FCSTD DOCUMENT  (FreeCAD 0.20R29177 (Git))
Label: Top Controls
License: All rights reserved
LicenseURL: http://en.wikipedia.org/wiki/All_rights_reserved
objects: App::Link×5, App::DocumentObjectGroup×3, PartDesign::CoordinateSystem×1, App::FeaturePython×1, App::Part×1
note: 1 computed .brp shape members not serialized (recipe doc carries the construction recipe); baked Part::Feature solids carry a one-line shape summary decoded from their .brp
EXTERNAL_REF file=Top Plate.FCStd obj=LCS_Origin
EXTERNAL_REF file=Top Plate.FCStd obj=Body
EXTERNAL_REF file=Potentiometers.FCStd obj=LCS_Origin
EXTERNAL_REF file=Top Plate.FCStd obj=LCS_Potentiometers
EXTERNAL_REF file=Potentiometers.FCStd obj=Assembly
EXTERNAL_REF file=Silder.FCStd obj=LCS_Origin
EXTERNAL_REF file=Top Plate.FCStd obj=LCS_Slider
EXTERNAL_REF file=Silder.FCStd obj=Model
EXTERNAL_REF file=LCD-1.28inch.FCStd obj=LCS_Origin
EXTERNAL_REF file=Top Plate.FCStd obj=LCS_LCD
EXTERNAL_REF file=LCD-1.28inch.FCStd obj=Model
EXTERNAL_REF file=Dsub.FCStd obj=LCS_TOP
EXTERNAL_REF file=Top Plate.FCStd obj=LCS_Dsub
EXTERNAL_REF file=Dsub.FCStd obj=Body

FEATURE [App::DocumentObjectGroup] Parts
FEATURE [PartDesign::CoordinateSystem] LCS_Origin
  AttacherType = Attacher::AttachEngine3D
  MapMode = 2
  Support = -> [X_Axis]
FEATURE [App::DocumentObjectGroup] Constraints
FEATURE [App::FeaturePython] Variables  # WARN: FeaturePython — macro-defined, semantics opaque (R4)
  Type = App::PropertyContainer
FEATURE [App::DocumentObjectGroup] Configurations
FEATURE [App::Link] Top_Plate  label="Top Plate"
  AttachedBy = #LCS_Origin
  AttachedTo = Parent Assembly#LCS_Origin
  LinkedObject = -> <external Top Plate.FCStd>#Body
  SolverId = Asm4EE
  expr: Placement = LCS_Origin.Placement * AttachmentOffset * Top_Plate#LCS_Origin.Placement ^ -1
FEATURE [App::Link] Potentiometers
  AttachedBy = #LCS_Origin
  AttachedTo = Top_Plate#LCS_Potentiometers
  AttachmentOffset = pos=(0,0,0) rot=(0,0,1;1.5708rad)
  LinkPlacement = pos=(30.5,29,2) rot=(0,-1,0;3.14159rad)
  LinkedObject = -> <external Potentiometers.FCStd>#Assembly
  Placement = pos=(30.5,29,2) rot=(0,-1,0;3.14159rad)
  SolverId = Asm4EE
  expr: Placement = Top_Plate.Placement * Top_Plate#LCS_Potentiometers.Placement * AttachmentOffset * Potentiometers#LCS_Origin.Placement ^ -1
FEATURE [App::Link] Silder  label="Slider"
  AttachedBy = #LCS_Origin
  AttachedTo = Top_Plate#LCS_Slider
  AttachmentOffset = pos=(0,0,0) rot=(0,1,0;3.14159rad)
  LinkPlacement = pos=(-30.5,0,2) rot=(0,1,0;3.14159rad)
  LinkedObject = -> <external Silder.FCStd>#Model
  Placement = pos=(-30.5,0,2) rot=(0,1,0;3.14159rad)
  SolverId = Asm4EE
  expr: Placement = Top_Plate.Placement * Top_Plate#LCS_Slider.Placement * AttachmentOffset * Silder#LCS_Origin.Placement ^ -1
FEATURE [App::Link] LCD
  AttachedBy = #LCS_Origin
  AttachedTo = Top_Plate#LCS_LCD
  AttachmentOffset = pos=(0,0,0) rot=(-1,0,0;3.14159rad)
  LinkPlacement = pos=(-61.75,-15.25,2) rot=(-1,0,0;3.14159rad)
  LinkedObject = -> <external LCD-1.28inch.FCStd>#Model
  Placement = pos=(-61.75,-15.25,2) rot=(-1,0,0;3.14159rad)
  SolverId = Asm4EE
  expr: Placement = Top_Plate.Placement * Top_Plate#LCS_LCD.Placement * AttachmentOffset * LCD_1_28inch#LCS_Origin.Placement ^ -1
FEATURE [App::Link] Dsub
  AttachedBy = #LCS_TOP
  AttachedTo = Top_Plate#LCS_Dsub
  AttachmentOffset = pos=(0,0,0) rot=(0,0,1;1.5708rad)
  LinkPlacement = pos=(32.5,-21,0) rot=(0,0,1;3.14159rad)
  LinkedObject = -> <external Dsub.FCStd>#Body
  Placement = pos=(32.5,-21,0) rot=(0,0,1;3.14159rad)
  SolverId = Asm4EE
  expr: Placement = Top_Plate.Placement * Top_Plate#LCS_Dsub.Placement * AttachmentOffset * Dsub#LCS_TOP.Placement ^ -1
FEATURE [App::Part] Model
  AssemblyType = Part::Link
  Group = -> [LCS_Origin,Constraints,Variables,Configurations,Top_Plate,Potentiometers,Silder,LCD,Dsub]
  Origin = -> Origin
  Type = Assembly

RESOLVED EXTERNAL PARTS (link-assembly join: the EXTERNAL_REF files above that resolve inside this repo's crawl, each included once):
---- part Dsub.FCStd = doc fcstd_46d8f76f5e4a ----
FCSTD DOCUMENT  (FreeCAD 0.20R29177 (Git))
Label: Dsub
License: All rights reserved
LicenseURL: https://en.wikipedia.org/wiki/All_rights_reserved
objects: Sketcher::SketchObject×2, PartDesign::Pad×1, PartDesign::Pocket×1, PartDesign::CoordinateSystem×1, PartDesign::Body×1
note: 8 computed .brp shape members not serialized (recipe doc carries the construction recipe); baked Part::Feature solids carry a one-line shape summary decoded from their .brp

FEATURE [Sketcher::SketchObject] Sketch
  FullyConstrained = true
  MapMode = 5
  Support = -> [XY_Plane]
  sketch-geometry (4):
    g0: LineSegment StartX=-35 StartY=15 StartZ=0 EndX=35 EndY=15 EndZ=0
    g1: LineSegment StartX=35 StartY=15 StartZ=0 EndX=35 EndY=-15 EndZ=0
    g2: LineSegment StartX=35 StartY=-15 StartZ=0 EndX=-35 EndY=-15 EndZ=0
    g3: LineSegment StartX=-35 StartY=-15 StartZ=0 EndX=-35 EndY=15 EndZ=0
  constraints (11):
    c: Coincident(g0,g1)
    c: Coincident(g1,g2)
    c: Coincident(g2,g3)
    c: Coincident(g3,g0)
    c: Horizontal(g0)
    c: Horizontal(g2)
    c: Vertical(g1)
    c: Vertical(g3)
    c: Symmetric(g0,g1,g-1)
    c: DistanceX(g0,g0) = 70
    c: DistanceY(g1,g1) = 30
FEATURE [PartDesign::Pad] Pad  label="Plate"
  Direction = (0,0,1)
  Length = 2
  Length2 = 10
  Profile = -> Sketch
  ReferenceAxis = -> Sketch [N_Axis]
  Refine = true
  Type = 0
FEATURE [Sketcher::SketchObject] Sketch001
  FullyConstrained = true
  MapMode = 5
  Support = -> [XY_Plane]
  sketch-geometry (6):
    g0: LineSegment StartX=-27.25 StartY=6.25 StartZ=0 EndX=27.25 EndY=6.25 EndZ=0
    g1: LineSegment StartX=27.25 StartY=6.25 StartZ=0 EndX=27.25 EndY=-6.25 EndZ=0
    g2: LineSegment StartX=27.25 StartY=-6.25 StartZ=0 EndX=-27.25 EndY=-6.25 EndZ=0
    g3: LineSegment StartX=-27.25 StartY=-6.25 StartZ=0 EndX=-27.25 EndY=6.25 EndZ=0
    g4: Circle CenterX=-30.555 CenterY=0 CenterZ=0 NormalX=0 NormalY=0 NormalZ=1 AngleXU=0 Radius=1.5
    g5: Circle CenterX=30.555 CenterY=1e-16 CenterZ=0 NormalX=0 NormalY=0 NormalZ=1 AngleXU=0 Radius=1.5
  constraints (16):
    c: Coincident(g0,g1)
    c: Coincident(g1,g2)
    c: Coincident(g2,g3)
    c: Coincident(g3,g0)
    c: Horizontal(g0)
    c: Horizontal(g2)
    c: Vertical(g1)
    c: Vertical(g3)
    c: Symmetric(g0,g1,g-1)
    c: DistanceX(g0,g0) = 54.5
    c: DistanceY(g1,g1) = 12.5
    c: PointOnObject(g4,g-1)
    c: Equal(g5,g4)
    c: Diameter(g4) = 3
    c: DistanceX(g4,g5) = 61.11
    c: Symmetric(g4,g5,g-1)
FEATURE [PartDesign::Pocket] Pocket  label="Holes"
  BaseFeature = -> Pad
  Direction = (0,0,-1)
  Length = 5
  Length2 = 5
  Profile = -> Sketch001
  ReferenceAxis = -> Sketch001 [N_Axis]
  Refine = true
  Reversed = true
  Type = 0
FEATURE [PartDesign::CoordinateSystem] LCS_TOP
  AttacherType = Attacher::AttachEngine3D
  AttachmentOffset = pos=(0,0,2) rot=(0,0,1;0rad)
  MapMode = 2
  Placement = pos=(0,0,2) rot=(0,0,1;0rad)
  Support = -> [Pad]
FEATURE [PartDesign::Body] Body
  Group = -> [Sketch,Pad,Sketch001,Pocket,LCS_TOP]
  Origin = -> Origin
  Tip = -> Pocket
---- part LCD-1.28inch.FCStd = doc fcstd_0bb850102ba9 ----
FCSTD DOCUMENT  (FreeCAD 0.20R29177 (Git))
Label: LCD-1.28inch
License: All rights reserved
LicenseURL: http://en.wikipedia.org/wiki/All_rights_reserved
objects: App::DocumentObjectGroup×3, PartDesign::CoordinateSystem×2, Part::FeaturePython×2, App::FeaturePython×1, Sketcher::SketchObject×1, PartDesign::Pad×1, PartDesign::Body×1, App::Link×1, App::Part×1
note: 8 computed .brp shape members not serialized (recipe doc carries the construction recipe); baked Part::Feature solids carry a one-line shape summary decoded from their .brp
EXTERNAL_REF file=LCD-1.28inch-Top.FCStd obj=LCS_Origin
EXTERNAL_REF file=LCD-1.28inch-Top.FCStd obj=Model
EXTERNAL_REF file=../../../.cache/FreeCAD/Cache/FreeCAD_Doc_ca71fdad-f997-481a-a821-e9ea57e04f97_da39a3_40904 obj=LCS_Origin
EXTERNAL_REF file=../../../.cache/FreeCAD/Cache/FreeCAD_Doc_ca71fdad-f997-481a-a821-e9ea57e04f97_da39a3_40904 obj=Assembly
EXTERNAL_REF file=Nut-Holder.FCStd obj=Assembly
EXTERNAL_REF file=../../../.cache/FreeCAD/Cache/FreeCAD_Doc_145d3813-2947-44bf-960b-8cda309f67ea_da39a3_40904 obj=LCS_Origin
EXTERNAL_REF file=../../../.cache/FreeCAD/Cache/FreeCAD_Doc_145d3813-2947-44bf-960b-8cda309f67ea_da39a3_40904 obj=Assembly

FEATURE [App::DocumentObjectGroup] Parts
FEATURE [PartDesign::CoordinateSystem] LCS_Origin
  AttacherType = Attacher::AttachEngine3D
  MapMode = 2
  Support = -> [X_Axis]
FEATURE [App::DocumentObjectGroup] Constraints
FEATURE [App::FeaturePython] Variables  # WARN: FeaturePython — macro-defined, semantics opaque (R4)
  Type = App::PropertyContainer
FEATURE [App::DocumentObjectGroup] Configurations
FEATURE [PartDesign::CoordinateSystem] LCS_0
  AttacherType = Attacher::AttachEngine3D
  MapMode = 2
  Support = -> [X_Axis001]
FEATURE [Sketcher::SketchObject] Sketch
  FullyConstrained = true
  MapMode = 5
  Support = -> [XY_Plane001]
  sketch-geometry (8):
    g0: ArcOfCircle CenterX=0 CenterY=0 CenterZ=0 NormalX=0 NormalY=0 NormalZ=1 AngleXU=0 Radius=18.5 StartAngle=5.18978 EndAngle=10.5182
    g1: LineSegment StartX=-8.5 StartY=-16.4317 StartZ=0 EndX=-7 EndY=-20.25 EndZ=0
    g2: LineSegment StartX=-7 StartY=-20.25 StartZ=0 EndX=7 EndY=-20.25 EndZ=0
    g3: LineSegment StartX=7 StartY=-20.25 StartZ=0 EndX=8.5 EndY=-16.4317 EndZ=0
    g4: LineSegment StartX=-20 StartY=30 StartZ=0 EndX=20 EndY=30 EndZ=0
    g5: LineSegment StartX=20 StartY=30 StartZ=0 EndX=20 EndY=-30 EndZ=0
    g6: LineSegment StartX=20 StartY=-30 StartZ=0 EndX=-20 EndY=-30 EndZ=0
    g7: LineSegment StartX=-20 StartY=-30 StartZ=0 EndX=-20 EndY=30 EndZ=0
  constraints (22):
    c: Coincident(g0,g-1)
    c: Coincident(g1,g0)
    c: Coincident(g2,g1)
    c: Coincident(g3,g2)
    c: Coincident(g3,g0)
    c: DistanceX(g0,g0) = 17
    c: Diameter(g0) = 37
    c: Horizontal(g0,g0)
    c: DistanceX(g2,g2) = 14
    c: Symmetric(g2,g1,g-2)
    c: DistanceY(g2,g0) = 20.25
    c: Coincident(g4,g5)
    c: Coincident(g5,g6)
    c: Coincident(g6,g7)
    c: Coincident(g7,g4)
    c: Horizontal(g4)
    c: Horizontal(g6)
    c: Vertical(g5)
    c: Vertical(g7)
    c: Symmetric(g5,g4,g0)
    c: DistanceY(g7,g7) = 60
    c: DistanceX(g4,g4) = 40
FEATURE [PartDesign::Pad] Pad
  Direction = (0,0,1)
  Length = 2
  Length2 = 10
  Profile = -> Sketch
  ReferenceAxis = -> Sketch [N_Axis]
  Type = 0
FEATURE [PartDesign::Body] Body
  Group = -> [LCS_0,Sketch,Pad]
  Origin = -> Origin001
  Tip = -> Pad
FEATURE [App::Link] LCD_1_28inch_Top
  AttachedBy = #LCS_Origin
  AttachedTo = Parent Assembly#LCS_Origin
  AttachmentOffset = pos=(0,0,6) rot=(0,0,1;0rad)
  LinkPlacement = pos=(0,0,6) rot=(0,0,1;0rad)
  LinkedObject = -> <external LCD-1.28inch-Top.FCStd>#Model
  Placement = pos=(0,0,6) rot=(0,0,1;0rad)
  SolverId = Asm4EE
  expr: Placement = LCS_Origin.Placement * AttachmentOffset * LCD_1_28inch_Top#LCS_Origin.Placement ^ -1
FEATURE [Part::FeaturePython] Nut_Holder_Bottom  # link proxy (typed FeaturePython)
  AttachedBy = #LCS_Origin
  AttachedTo = Parent Assembly#LCS_Origin
  AttachmentOffset = pos=(0,-30,1.2) rot=(0,0,1;0rad)
  LinkedObject = -> <external ../../../.cache/FreeCAD/Cache/FreeCAD_Doc_ca71fdad-f997-481a-a821-e9ea57e04f97_da39a3_40904>#Assembly
  Placement = pos=(0,-30,1.2) rot=(0,0,1;0rad)
  SolverId = Asm4EE
  SourceObject = -> <external Nut-Holder.FCStd>#Assembly
  Type = Asm4::VariantLink
  diameter = 8.6
  height = 4.8
  nut_width = 6
  pocket_height = 4.8
  expr: Placement = LCS_Origin.Placement * AttachmentOffset * varTmpDoc_11#LCS_Origin.Placement ^ -1
FEATURE [Part::FeaturePython] Nut_Holder_Top  # link proxy (typed FeaturePython)
  AttachedBy = #LCS_Origin
  AttachedTo = Parent Assembly#LCS_Origin
  AttachmentOffset = pos=(0,25,1.2) rot=(0,0,1;0rad)
  LinkedObject = -> <external ../../../.cache/FreeCAD/Cache/FreeCAD_Doc_145d3813-2947-44bf-960b-8cda309f67ea_da39a3_40904>#Assembly
  Placement = pos=(0,25,1.2) rot=(0,0,1;0rad)
  SolverId = Asm4EE
  SourceObject = -> <external Nut-Holder.FCStd>#Assembly
  Type = Asm4::VariantLink
  diameter = 8.6
  height = 4.8
  nut_width = 6
  pocket_height = 4.8
  expr: Placement = LCS_Origin.Placement * AttachmentOffset * varTmpDoc_12#LCS_Origin.Placement ^ -1
FEATURE [App::Part] Model
  AssemblyType = Part::Link
  Group = -> [LCS_Origin,Constraints,Variables,Configurations,Body,LCD_1_28inch_Top,Nut_Holder_Bottom,Nut_Holder_Top]
  Origin = -> Origin
  Type = Assembly
---- part Potentiometers.FCStd = doc fcstd_f381ef1390fa ----
FCSTD DOCUMENT  (FreeCAD 0.20R29410 (Git))
Label: Potentiometers
License: All rights reserved
LicenseURL: https://en.wikipedia.org/wiki/All_rights_reserved
objects: App::DocumentObjectGroup×3, App::Link×2, PartDesign::CoordinateSystem×1, App::FeaturePython×1, App::Part×1
note: 1 computed .brp shape members not serialized (recipe doc carries the construction recipe); baked Part::Feature solids carry a one-line shape summary decoded from their .brp
EXTERNAL_REF file=Potentiometer-Base.FCStd obj=LCS_Origin
EXTERNAL_REF file=Potentiometer-Base.FCStd obj=Assembly
EXTERNAL_REF file=Potentiometers-Top.FCStd obj=LCS_Origin
EXTERNAL_REF file=Potentiometers-Top.FCStd obj=Assembly

FEATURE [App::DocumentObjectGroup] Parts
FEATURE [PartDesign::CoordinateSystem] LCS_Origin
  AttacherType = Attacher::AttachEngine3D
  MapMode = 2
  Support = -> [X_Axis]
FEATURE [App::DocumentObjectGroup] Constraints
FEATURE [App::FeaturePython] Variables  # WARN: FeaturePython — macro-defined, semantics opaque (R4)
  Type = App::PropertyContainer
FEATURE [App::DocumentObjectGroup] Configurations
FEATURE [App::Link] Potentiometer_Base
  AttachedBy = #LCS_Origin
  AttachedTo = Parent Assembly#LCS_Origin
  LinkedObject = -> <external Potentiometer-Base.FCStd>#Assembly
  SolverId = Asm4EE
  expr: Placement = LCS_Origin.Placement * AttachmentOffset * Potentiometer_Base#LCS_Origin.Placement ^ -1
FEATURE [App::Link] Potentiometers_Top
  AttachedBy = #LCS_Origin
  AttachedTo = Parent Assembly#LCS_Origin
  AttachmentOffset = pos=(0,0,11.2) rot=(0,0,1;0rad)
  LinkPlacement = pos=(0,0,11.2) rot=(0,0,1;0rad)
  LinkedObject = -> <external Potentiometers-Top.FCStd>#Assembly
  Placement = pos=(0,0,11.2) rot=(0,0,1;0rad)
  SolverId = Asm4EE
  expr: Placement = LCS_Origin.Placement * AttachmentOffset * Potentiometers_Top#LCS_Origin.Placement ^ -1
FEATURE [App::Part] Assembly
  AssemblyType = Part::Link
  Group = -> [LCS_Origin,Constraints,Variables,Configurations,Potentiometer_Base,Potentiometers_Top]
  Origin = -> Origin
  Type = Assembly
---- part Silder.FCStd = doc fcstd_1cb2370d0617 ----
FCSTD DOCUMENT  (FreeCAD 0.20R29410 (Git))
Label: Silder
License: All rights reserved
LicenseURL: http://en.wikipedia.org/wiki/All_rights_reserved
objects: PartDesign::CoordinateSystem×4, App::DocumentObjectGroup×3, Part::FeaturePython×2, App::FeaturePython×1, Sketcher::SketchObject×1, PartDesign::Pad×1, PartDesign::Body×1, App::Part×1
note: 10 computed .brp shape members not serialized (recipe doc carries the construction recipe); baked Part::Feature solids carry a one-line shape summary decoded from their .brp
EXTERNAL_REF file=../../../../.cache/FreeCAD/Cache/FreeCAD_Doc_b944a62a-5acd-4748-8a46-371a6e0a0b2d_da39a3_75311 obj=LCS_Origin
EXTERNAL_REF file=../../../../.cache/FreeCAD/Cache/FreeCAD_Doc_b944a62a-5acd-4748-8a46-371a6e0a0b2d_da39a3_75311 obj=Assembly
EXTERNAL_REF file=Nut-Holder.FCStd obj=Assembly
EXTERNAL_REF file=../../../../.cache/FreeCAD/Cache/FreeCAD_Doc_43aa0dcd-2b8e-4044-a69a-189f3c988842_da39a3_75311 obj=LCS_Origin
EXTERNAL_REF file=../../../../.cache/FreeCAD/Cache/FreeCAD_Doc_43aa0dcd-2b8e-4044-a69a-189f3c988842_da39a3_75311 obj=Assembly

FEATURE [App::DocumentObjectGroup] Parts
FEATURE [PartDesign::CoordinateSystem] LCS_Origin
  AttacherType = Attacher::AttachEngine3D
  MapMode = 2
  Support = -> [X_Axis]
FEATURE [App::DocumentObjectGroup] Constraints
FEATURE [App::FeaturePython] Variables  # WARN: FeaturePython — macro-defined, semantics opaque (R4)
  Type = App::PropertyContainer
FEATURE [App::DocumentObjectGroup] Configurations
FEATURE [PartDesign::CoordinateSystem] LCS_0
  AttacherType = Attacher::AttachEngine3D
  MapMode = 2
  Support = -> [X_Axis001]
FEATURE [Sketcher::SketchObject] Sketch
  FullyConstrained = true
  MapMode = 5
  Support = -> [XY_Plane001]
  sketch-geometry (8):
    g0: LineSegment StartX=-10.5 StartY=45 StartZ=0 EndX=10.5 EndY=45 EndZ=0
    g1: LineSegment StartX=10.5 StartY=45 StartZ=0 EndX=10.5 EndY=-45 EndZ=0
    g2: LineSegment StartX=10.5 StartY=-45 StartZ=0 EndX=-10.5 EndY=-45 EndZ=0
    g3: LineSegment StartX=-10.5 StartY=-45 StartZ=0 EndX=-10.5 EndY=45 EndZ=0
    g4: LineSegment StartX=-5 StartY=37.5 StartZ=0 EndX=-2 EndY=37.5 EndZ=0
    g5: LineSegment StartX=-2 StartY=37.5 StartZ=0 EndX=-2 EndY=-37.5 EndZ=0
    g6: LineSegment StartX=-2 StartY=-37.5 StartZ=0 EndX=-5 EndY=-37.5 EndZ=0
    g7: LineSegment StartX=-5 StartY=-37.5 StartZ=0 EndX=-5 EndY=37.5 EndZ=0
  constraints (23):
    c: Coincident(g0,g1)
    c: Coincident(g1,g2)
    c: Coincident(g2,g3)
    c: Coincident(g3,g0)
    c: Horizontal(g0)
    c: Horizontal(g2)
    c: Vertical(g1)
    c: Vertical(g3)
    c: Symmetric(g0,g1,g-1)
    c: DistanceY(g1,g1) = 90
    c: DistanceX(g0,g0) = 21
    c: Coincident(g4,g5)
    c: Coincident(g5,g6)
    c: Coincident(g6,g7)
    c: Coincident(g7,g4)
    c: Horizontal(g4)
    c: Horizontal(g6)
    c: Vertical(g5)
    c: Vertical(g7)
    c: DistanceY(g7,g7) = 75
    c: DistanceX(g4,g4) = 3
    c: DistanceX(g2,g6) = 5.5
    c: DistanceY(g2,g6) = 7.5
FEATURE [PartDesign::Pad] Pad
  Direction = (0,0,1)
  Length = 2
  Length2 = 10
  Profile = -> Sketch
  ReferenceAxis = -> Sketch [N_Axis]
  Type = 0
FEATURE [PartDesign::Body] Body
  Group = -> [LCS_0,Sketch,Pad]
  Origin = -> Origin001
  Tip = -> Pad
FEATURE [PartDesign::CoordinateSystem] LCS_TL_Nut_Holder
  AttacherType = Attacher::AttachEngine3D
  AttachmentOffset = pos=(-3,3,0) rot=(0,0,1;0rad)
  MapMode = 6
  Placement = pos=(-7.5,42,2) rot=(0,0,1;3.14159rad)
  Support = -> [Pad]
FEATURE [PartDesign::CoordinateSystem] LCS_BR_Nut_Holder
  AttacherType = Attacher::AttachEngine3D
  AttachmentOffset = pos=(3,-3,0) rot=(0,0,1;0rad)
  MapMode = 6
  Placement = pos=(7.5,-42,2) rot=(0,0,1;3.14159rad)
  Support = -> [Pad]
FEATURE [Part::FeaturePython] Nut_Holder_TL  # link proxy (typed FeaturePython)
  AttachedBy = #LCS_Origin
  AttachedTo = Parent Assembly#LCS_TL_Nut_Holder
  LinkedObject = -> <external ../../../../.cache/FreeCAD/Cache/FreeCAD_Doc_b944a62a-5acd-4748-8a46-371a6e0a0b2d_da39a3_75311>#Assembly
  Placement = pos=(-7.5,42,2) rot=(0,0,1;3.14159rad)
  SolverId = Asm4EE
  SourceObject = -> <external Nut-Holder.FCStd>#Assembly
  Type = Asm4::VariantLink
  diameter = 8.6
  height = 9.2
  nut_width = 6
  pocket_height = 4.8
  expr: Placement = LCS_TL_Nut_Holder.Placement * AttachmentOffset * varTmpDoc_3#LCS_Origin.Placement ^ -1
FEATURE [Part::FeaturePython] Nut_Holder_BR  # link proxy (typed FeaturePython)
  AttachedBy = #LCS_Origin
  AttachedTo = Parent Assembly#LCS_BR_Nut_Holder
  LinkedObject = -> <external ../../../../.cache/FreeCAD/Cache/FreeCAD_Doc_43aa0dcd-2b8e-4044-a69a-189f3c988842_da39a3_75311>#Assembly
  Placement = pos=(7.5,-42,2) rot=(0,0,1;3.14159rad)
  SolverId = Asm4EE
  SourceObject = -> <external Nut-Holder.FCStd>#Assembly
  Type = Asm4::VariantLink
  diameter = 8.6
  height = 9.2
  nut_width = 6
  pocket_height = 4.8
  expr: Placement = LCS_BR_Nut_Holder.Placement * AttachmentOffset * varTmpDoc_4#LCS_Origin.Placement ^ -1
FEATURE [App::Part] Model
  AssemblyType = Part::Link
  Group = -> [LCS_Origin,Constraints,Variables,Configurations,Body,LCS_TL_Nut_Holder,LCS_BR_Nut_Holder,Nut_Holder_TL,Nut_Holder_BR]
  Origin = -> Origin
  Type = Assembly
